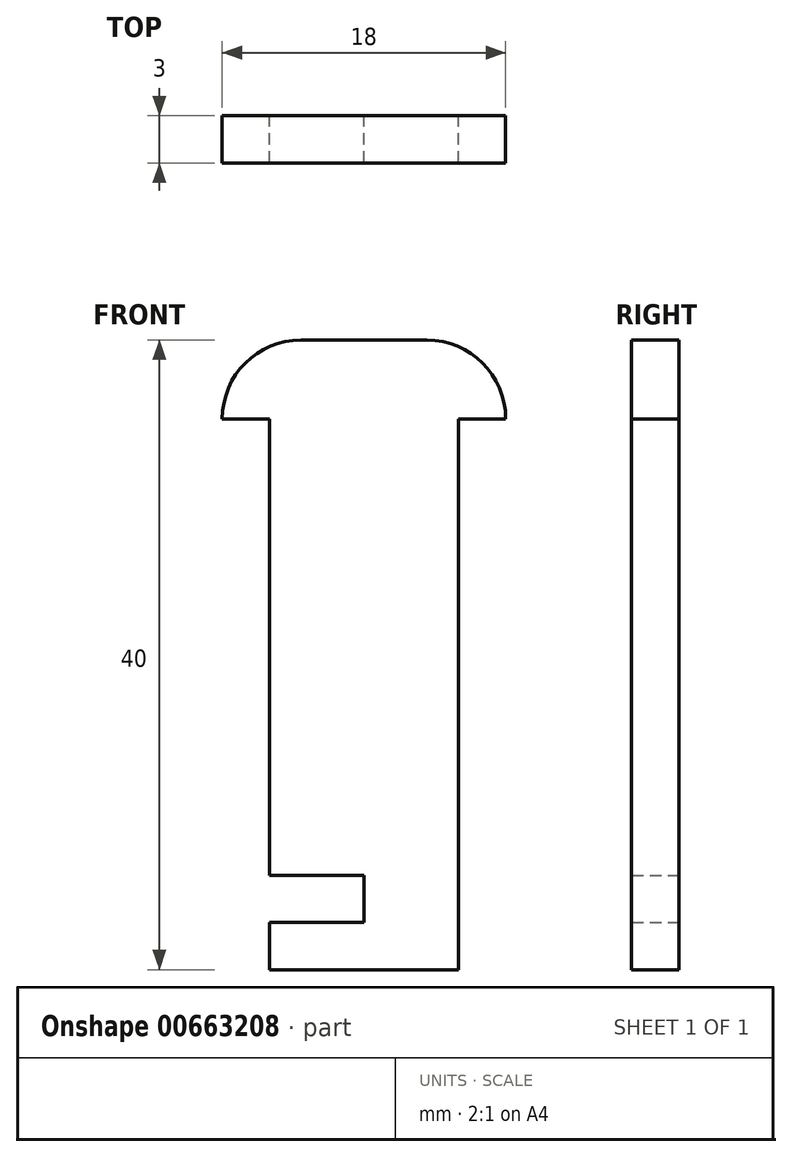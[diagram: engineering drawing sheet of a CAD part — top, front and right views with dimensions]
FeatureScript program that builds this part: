
annotation { "Feature Type Name" : "Feature", "Feature Type Description" : "" }
export const myFeature = defineFeature(function(context is Context, id is Id, definition is map)
    precondition{}
    {
        {
            var Q0;
            Q0=qCreatedBy(makeId("Front.planeOp"),FACE);
            var sketch = newSketch(context, id + "F0", { "sketchPlane" : qUnion([Q0])});
            skLineSegment(sketch, "E0", {"start": v(-6, 29) * mm, "end": v(-6, 0) * mm});
            skLineSegment(sketch, "E1", {"start": v(-6, 0) * mm, "end": v(0, 0) * mm});
            skLineSegment(sketch, "E2", {"start": v(0, 0) * mm, "end": v(0, -3) * mm});
            skLineSegment(sketch, "E3", {"start": v(0, -3) * mm, "end": v(-6, -3) * mm});
            skLineSegment(sketch, "E4", {"start": v(-6, -3) * mm, "end": v(-6, -6) * mm});
            skLineSegment(sketch, "E5", {"start": v(-6, -6) * mm, "end": v(6, -6) * mm});
            skLineSegment(sketch, "E6", {"start": v(6, -6) * mm, "end": v(6, 29) * mm});
            skLineSegment(sketch, "E7", {"start": v(6, 29) * mm, "end": v(9, 29) * mm});
            skLineSegment(sketch, "E8", {"start": v(9, 29) * mm, "end": v(9, 29) * mm});
            skLineSegment(sketch, "E9", {"start": v(4, 34) * mm, "end": v(-4, 34) * mm});
            skLineSegment(sketch, "E10", {"start": v(-9, 29) * mm, "end": v(-9, 29) * mm});
            skLineSegment(sketch, "E11", {"start": v(-9, 29) * mm, "end": v(-6, 29) * mm});
            skPoint(sketch, "E12.visualSharp", {"position": v(-9, 34) * mm});
            skArc(sketch, "E12.filletArc", {"start": v(-4, 34) * mm, "mid": v(-7.54, 32.54) * mm, "end": v(-9, 29) * mm});
            skPoint(sketch, "E13.visualSharp", {"position": v(9, 34) * mm});
            skArc(sketch, "E13.filletArc", {"start": v(9, 29) * mm, "mid": v(7.54, 32.54) * mm, "end": v(4, 34) * mm});
            skSolve(sketch);
        }
        {
            var Q0;
            Q0=qSketchRegion(id+"F0",true);
            extrude(context, id + "F1", {"entities" : qUnion([Q0]), "depth" : 3 * mm, "offsetDistance" : 25 * mm});
        }
    });
